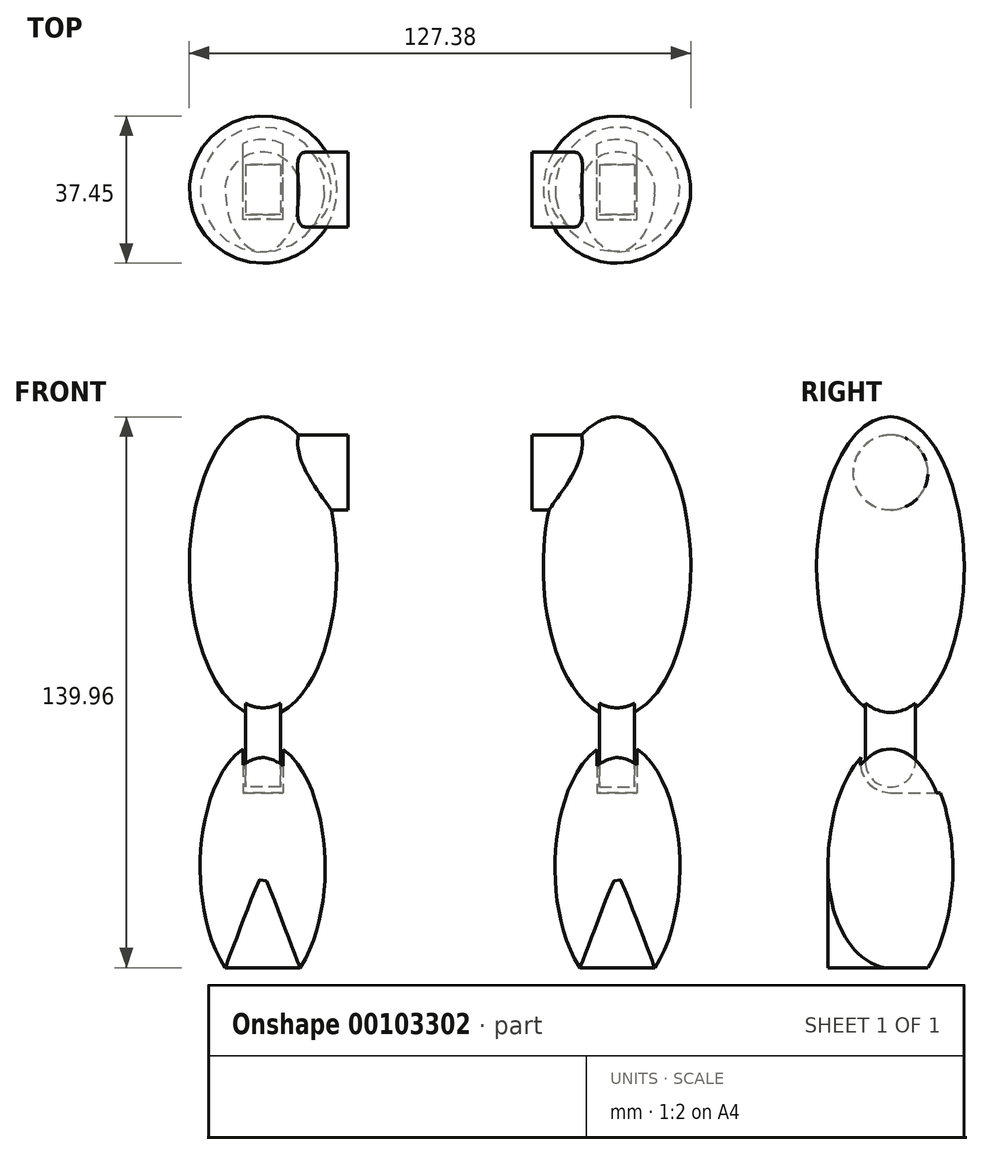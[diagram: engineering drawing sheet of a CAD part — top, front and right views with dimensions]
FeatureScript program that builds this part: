
annotation { "Feature Type Name" : "Feature", "Feature Type Description" : "" }
export const myFeature = defineFeature(function(context is Context, id is Id, definition is map)
    precondition{}
    {
        {
            var Q0;
            Q0=qCreatedBy(makeId("Front.planeOp"),FACE);
            var sketch = newSketch(context, id + "F0", { "sketchPlane" : qUnion([Q0])});
            skEllipticalArc(sketch, "E0", {});
            skLineSegment(sketch, "E1", {"start": v(-45.07, -25.4) * mm, "end": v(-35.54, -25.4) * mm});
            skLineSegment(sketch, "E2", {"start": v(-45.07, -25.4) * mm, "end": v(-45.07, 31.75) * mm});
            skPoint(sketch, "E3.orphan", {"position": v(-54.6, -25.4) * mm});
            const initialGuessF0  = {"E0": [-0.04506855830550194, 0, 0, -1, 0.03175, 0.015875, 0.6435011087932844, 3.141592653589793]};
            skSetInitialGuess(sketch, initialGuessF0);
            skSolve(sketch);
        }
        {
            var Q0;
            Q0=makeQuery(id+"F0.imprint","IMPRINT",FACE,{"disambiguationData":[TD([[makeQuery(id+"F0.imprint","IMPRINT",EDGE,{"derivedFrom":sQuery(id+"F0.wireOp",EDGE,"E0")}),1.0]])]});
            var Q1;
            Q1=sQuery(id+"F0.wireOp",EDGE,"E2");
            revolve(context, id + "F1", {"entities" : qUnion([Q0]), "axis" : qUnion([Q1]), "revolveType" : RevolveType.FULL});
        }
        {
            var Q0;
            Q0=qCreatedBy(makeId("Top.planeOp"),FACE);
            cPlane(context, id + "F2", {"entities" : qUnion([Q0]), "cplaneType" : CPlaneType.OFFSET, "offset" : 25.4 * mm, "oppositeDirection" : true, "width" : 152.4 * mm, "height" : 152.4 * mm});
        }
        {
            var Q0;
            Q0=qCreatedBy(id+"F2.planeOp",FACE);
            var sketch = newSketch(context, id + "F3", { "sketchPlane" : qUnion([Q0])});
            skEllipticalArc(sketch, "E4", {});
            skLineSegment(sketch, "E5", {"start": v(-54.55, 0) * mm, "end": v(-35.59, 0) * mm});
            const initialGuessF3  = {"E4": [-0.04506855830550194, 0, 0, -1, 0.015834808349609375, 0.009479845533347077, 4.71238898038469, 1.5707963267948966]};
            skSetInitialGuess(sketch, initialGuessF3);
            skSolve(sketch);
        }
        {
            var Q0;
            Q0=makeQuery(id+"F3.imprint","IMPRINT",FACE,{"disambiguationData":[TD([[makeQuery(id+"F3.imprint","IMPRINT",EDGE,{"derivedFrom":sQuery(id+"F3.wireOp",EDGE,"E4")}),1.0]])]});
            extrude(context, id + "F4", {"entities" : qUnion([Q0]), "operationType" : NewBodyOperationType.ADD, "depth" : 25.4 * mm});
        }
        {
            var Q0;
            Q0=qCreatedBy(makeId("Right.planeOp"),FACE);
            cPlane(context, id + "F5", {"entities" : qUnion([Q0]), "cplaneType" : CPlaneType.OFFSET, "offset" : 44.96 * mm, "oppositeDirection" : true, "width" : 152.4 * mm, "height" : 152.4 * mm});
        }
        {
            var Q0;
            Q0=qCreatedBy(id+"F5.planeOp",FACE);
            var sketch = newSketch(context, id + "F6", { "sketchPlane" : qUnion([Q0])});
            skArc(sketch, "E6", {"start": v(0, 34.3) * mm, "mid": v(-7.62, 26.67) * mm, "end": v(0, 19.05) * mm});
            skLineSegment(sketch, "E7.bottom", {"start": v(0, 19.05) * mm, "end": v(14.24, 19.05) * mm});
            skLineSegment(sketch, "E7.top", {"start": v(0, 34.35) * mm, "end": v(14.24, 34.35) * mm});
            skLineSegment(sketch, "E7.right", {"start": v(14.24, 19.05) * mm, "end": v(14.24, 34.35) * mm});
            skLineSegment(sketch, "E8.trimOffspring", {"start": v(0, 34.3) * mm, "end": v(0, 34.35) * mm});
            skSolve(sketch);
        }
        {
            var Q0;
            Q0 = qSketchRegion(id + "F6", true);
            extrude(context, id + "F7", {"entities" : qUnion([Q0]), "operationType" : NewBodyOperationType.REMOVE, "endBound" : BoundingType.SYMMETRIC, "depth" : 10.16 * mm});
        }
        {
            var Q0;
            Q0=qCreatedBy(id+"F5.planeOp",FACE);
            var sketch = newSketch(context, id + "F8", { "sketchPlane" : qUnion([Q0])});
            skArc(sketch, "E9", {"start": v(-6.35, 26.83) * mm, "mid": v(0, 20.48) * mm, "end": v(6.35, 26.83) * mm});
            skArc(sketch, "E10", {"start": v(6.35, 47.15) * mm, "mid": v(0, 53.5) * mm, "end": v(-6.35, 47.15) * mm});
            skLineSegment(sketch, "E11.left", {"start": v(6.35, 47.15) * mm, "end": v(6.35, 26.83) * mm});
            skLineSegment(sketch, "E11.right", {"start": v(-6.35, 47.15) * mm, "end": v(-6.35, 26.83) * mm});
            skSolve(sketch);
        }
        {
            var Q0;
            Q0 = qSketchRegion(id + "F8", true);
            extrude(context, id + "F9", {"entities" : qUnion([Q0]), "endBound" : BoundingType.SYMMETRIC, "depth" : 8.9 * mm});
        }
        {
            var Q0;
            Q0=qCreatedBy(id+"F5.planeOp",FACE);
            var sketch = newSketch(context, id + "F10", { "sketchPlane" : qUnion([Q0])});
            skEllipticalArc(sketch, "E12", {});
            skLineSegment(sketch, "E13", {"start": v(0, 38.36) * mm, "end": v(0, 114.56) * mm});
            const initialGuessF10  = {"E12": [0, 0.07646314799785614, 0, -1, 0.0381, 0.018732500000000003, 3.141592653589793, 0]};
            skSetInitialGuess(sketch, initialGuessF10);
            skSolve(sketch);
        }
        {
            var Q0;
            Q0=makeQuery(id+"F10.imprint","IMPRINT",FACE,{"disambiguationData":[TD([[makeQuery(id+"F10.imprint","IMPRINT",EDGE,{"derivedFrom":sQuery(id+"F10.wireOp",EDGE,"E12")}),1.0]])]});
            var Q1;
            Q1=sQuery(id+"F10.wireOp",EDGE,"E13");
            revolve(context, id + "F11", {"operationType" : NewBodyOperationType.ADD, "entities" : qUnion([Q0]), "axis" : qUnion([Q1]), "revolveType" : RevolveType.FULL});
        }
        {
            var Q0;
            Q0=qCreatedBy(id+"F5.planeOp",FACE);
            var sketch = newSketch(context, id + "F12", { "sketchPlane" : qUnion([Q0])});
            skCircle(sketch, "E14", {"center": v(0, 100.42) * mm, "radius": 9.53 * mm});
            skSolve(sketch);
        }
        {
            var Q0;
            Q0 = qSketchRegion(id + "F12", true);
            extrude(context, id + "F13", {"entities" : qUnion([Q0]), "operationType" : NewBodyOperationType.ADD, "depth" : 21.59 * mm});
        }
        {
            var Q0;
            Q0=makeQuery(id+"F1.opRevolve","SWEPT_BODY",BODY,{"disambiguationData":[OSD([sQuery(id+"F0.wireOp",EDGE,"E0"),sQuery(id+"F0.wireOp",EDGE,"E1"),sQuery(id+"F0.wireOp",EDGE,"E2")])]});
            var Q1;
            Q1=makeQuery(id+"F9.opExtrude","SWEPT_BODY",BODY,{"disambiguationData":[OSD([sQuery(id+"F8.wireOp",EDGE,"E9"),sQuery(id+"F8.wireOp",EDGE,"E10"),sQuery(id+"F8.wireOp",EDGE,"E11.left"),sQuery(id+"F8.wireOp",EDGE,"E11.right")])]});
            var Q2;
            Q2=qCreatedBy(makeId("Right.planeOp"),FACE);
            mirror(context, id + "F14", {"entities" : qUnion([Q0, Q1]), "mirrorPlane" : qUnion([Q2])});
        }
    });
